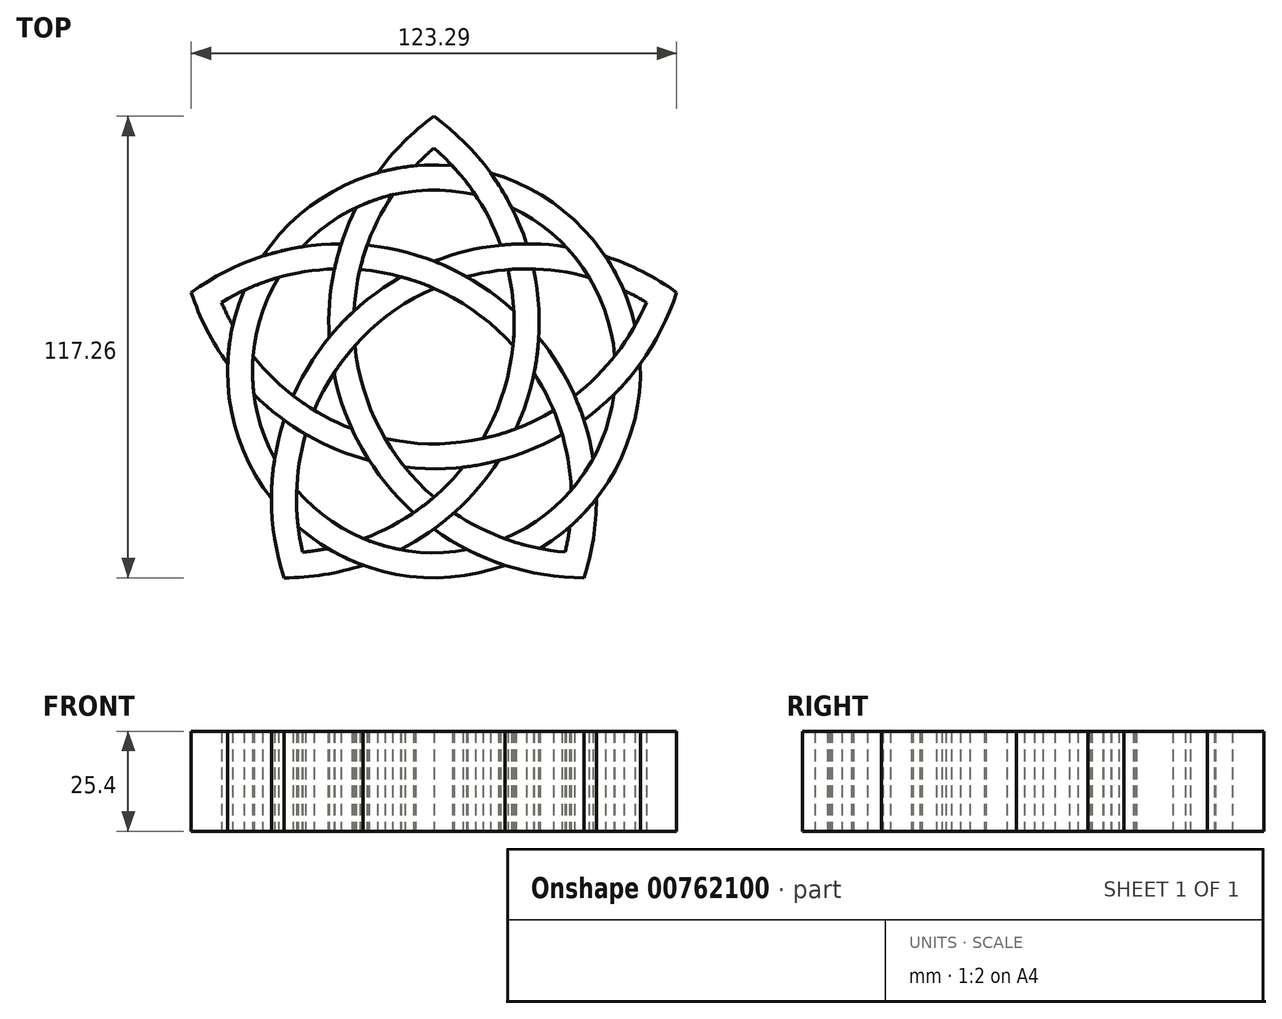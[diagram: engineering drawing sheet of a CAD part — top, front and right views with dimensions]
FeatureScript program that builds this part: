
annotation { "Feature Type Name" : "Feature", "Feature Type Description" : "" }
export const myFeature = defineFeature(function(context is Context, id is Id, definition is map)
    precondition{}
    {
        {
            var Q0;
            Q0=qCreatedBy(makeId("Top.planeOp"),FACE);
            var sketch = newSketch(context, id + "F0", { "sketchPlane" : qUnion([Q0])});
            skLineSegment(sketch, "E0", {"start": v(0, 72.47) * mm, "end": v(-61.65, 117.26) * mm, "construction": true});
            skLineSegment(sketch, "E1", {"start": v(-61.65, 117.26) * mm, "end": v(-123.3, 72.47) * mm, "construction": true});
            skLineSegment(sketch, "E2", {"start": v(-123.3, 72.47) * mm, "end": v(-99.75, 0) * mm, "construction": true});
            skLineSegment(sketch, "E3", {"start": v(-99.75, 0) * mm, "end": v(-23.55, 0) * mm, "construction": true});
            skLineSegment(sketch, "E4", {"start": v(0, 72.47) * mm, "end": v(-23.55, 0) * mm, "construction": true});
            skArc(sketch, "E5", {"start": v(-23.55, 0) * mm, "mid": v(-21.17, 9.92) * mm, "end": v(-20.37, 20.09) * mm});
            skArc(sketch, "E6", {"start": v(0, 72.47) * mm, "mid": v(-8.7, 77.8) * mm, "end": v(-18.13, 81.7) * mm});
            skArc(sketch, "E7", {"start": v(-99.75, 0) * mm, "mid": v(-89.58, 0.8) * mm, "end": v(-79.66, 3.2) * mm});
            skArc(sketch, "E8", {"start": v(-61.65, 117.26) * mm, "mid": v(-69.4, 110.63) * mm, "end": v(-76.02, 102.87) * mm});
            skArc(sketch, "E9", {"start": v(-123.3, 72.47) * mm, "mid": v(-119.39, 63.05) * mm, "end": v(-114.05, 54.35) * mm});
            skArc(sketch, "E10.0", {"start": v(-7.7, 69.97) * mm, "mid": v(-10.51, 71.58) * mm, "end": v(-13.42, 73.04) * mm});
            skArc(sketch, "E11.0", {"start": v(-28.3, 6.54) * mm, "mid": v(-27.64, 9.73) * mm, "end": v(-27.16, 12.94) * mm});
            skArc(sketch, "E12.0", {"start": v(-61.65, 109.17) * mm, "mid": v(-64.05, 106.99) * mm, "end": v(-66.33, 104.67) * mm});
            skArc(sketch, "E13.0", {"start": v(-95, 6.54) * mm, "mid": v(-91.76, 6.9) * mm, "end": v(-88.56, 7.43) * mm});
            skArc(sketch, "E14.0", {"start": v(-115.6, 69.97) * mm, "mid": v(-114.27, 67) * mm, "end": v(-112.77, 64.12) * mm});
            skPoint(sketch, "E15.first.point", {"position": v(-99.75, 40.06) * mm});
            skPoint(sketch, "E15.second.point", {"position": v(-38.1, 84.85) * mm});
            skPoint(sketch, "E15.third.point", {"position": v(-23.55, 40.06) * mm});
            skArc(sketch, "E16", {"start": v(-51.14, 97.32) * mm, "mid": v(-74.92, 96.58) * mm, "end": v(-95.16, 84.08) * mm});
            skArc(sketch, "E17.0", {"start": v(-56.96, 104.67) * mm, "mid": v(-84.2, 99.78) * mm, "end": v(-105.17, 81.7) * mm});
            skArc(sketch, "E18.trimOffspring", {"start": v(-85.2, 84.85) * mm, "mid": v(-105.22, 81.68) * mm, "end": v(-123.3, 72.47) * mm});
            skArc(sketch, "E19.trimOffspring", {"start": v(-86.91, 78.47) * mm, "mid": v(-101.81, 76.09) * mm, "end": v(-115.6, 69.97) * mm});
            skArc(sketch, "E20.trimOffspring", {"start": v(-81.72, 58.96) * mm, "mid": v(-75.4, 37.78) * mm, "end": v(-61.65, 20.47) * mm});
            skArc(sketch, "E21.trimOffspring", {"start": v(-87.08, 51.96) * mm, "mid": v(-79.8, 32.6) * mm, "end": v(-66.78, 16.53) * mm});
            skArc(sketch, "E22.trimOffspring", {"start": v(-74.05, 35.36) * mm, "mid": v(-51.95, 34.84) * mm, "end": v(-31.24, 42.56) * mm});
            skArc(sketch, "E23.trimOffspring", {"start": v(-69.05, 28.1) * mm, "mid": v(-48.4, 29.05) * mm, "end": v(-29.08, 36.46) * mm});
            skArc(sketch, "E24.trimOffspring", {"start": v(-56.51, 16.53) * mm, "mid": v(-43.06, 9.7) * mm, "end": v(-28.3, 6.54) * mm});
            skArc(sketch, "E25.trimOffspring", {"start": v(-61.65, 12.38) * mm, "mid": v(-43.58, 3.17) * mm, "end": v(-23.55, 0) * mm});
            skArc(sketch, "E26.trimOffspring", {"start": v(-23.55, 40.06) * mm, "mid": v(-9.2, 54.4) * mm, "end": v(0, 72.47) * mm});
            skArc(sketch, "E27.trimOffspring", {"start": v(-25.9, 46.23) * mm, "mid": v(-15.25, 56.91) * mm, "end": v(-7.7, 69.97) * mm});
            skArc(sketch, "E28.trimOffspring", {"start": v(-41.35, 67.77) * mm, "mid": v(-58.62, 79.15) * mm, "end": v(-78.6, 84.51) * mm});
            skArc(sketch, "E29.trimOffspring", {"start": v(-41.57, 58.96) * mm, "mid": v(-59.14, 72.38) * mm, "end": v(-80.44, 78.3) * mm});
            skArc(sketch, "E30.trimOffspring", {"start": v(-61.65, 73.55) * mm, "mid": v(-79.83, 60.98) * mm, "end": v(-92.05, 42.56) * mm});
            skArc(sketch, "E31.trimOffspring", {"start": v(-69.96, 76.48) * mm, "mid": v(-86.12, 63.57) * mm, "end": v(-97.39, 46.23) * mm});
            skArc(sketch, "E32.trimOffspring", {"start": v(-99.75, 40.06) * mm, "mid": v(-102.92, 20.03) * mm, "end": v(-99.75, 0) * mm});
            skArc(sketch, "E33.trimOffspring", {"start": v(-94.21, 36.46) * mm, "mid": v(-96.55, 21.55) * mm, "end": v(-95, 6.54) * mm});
            skArc(sketch, "E34.trimOffspring", {"start": v(-49.24, 35.36) * mm, "mid": v(-41.91, 56.22) * mm, "end": v(-42.85, 78.3) * mm});
            skArc(sketch, "E35.trimOffspring", {"start": v(-40.8, 37.88) * mm, "mid": v(-35.3, 57.82) * mm, "end": v(-36.38, 78.47) * mm});
            skArc(sketch, "E36.trimOffspring", {"start": v(-38.1, 84.85) * mm, "mid": v(-47.3, 102.92) * mm, "end": v(-61.65, 117.26) * mm});
            skArc(sketch, "E37.trimOffspring", {"start": v(-44.7, 84.51) * mm, "mid": v(-51.57, 97.95) * mm, "end": v(-61.65, 109.17) * mm});
            skArc(sketch, "E38.trimOffspring", {"start": v(-72.15, 97.32) * mm, "mid": v(-79.05, 83.2) * mm, "end": v(-81.94, 67.77) * mm});
            skArc(sketch, "E39.trimOffspring", {"start": v(-81.38, 94.1) * mm, "mid": v(-87, 78.04) * mm, "end": v(-88.26, 61.09) * mm});
            skArc(sketch, "E40.trimOffspring", {"start": v(-101.08, 76.3) * mm, "mid": v(-107.73, 53.46) * mm, "end": v(-102.1, 30.34) * mm});
            skArc(sketch, "E41.trimOffspring", {"start": v(-109.87, 73.04) * mm, "mid": v(-113.64, 45.61) * mm, "end": v(-102.92, 20.09) * mm});
            skArc(sketch, "E42.trimOffspring", {"start": v(-107.57, 56.32) * mm, "mid": v(-96.29, 45.4) * mm, "end": v(-82.5, 37.88) * mm});
            skArc(sketch, "E43.trimOffspring", {"start": v(-107.36, 46.54) * mm, "mid": v(-93.83, 36.24) * mm, "end": v(-78.1, 29.8) * mm});
            skArc(sketch, "E44.trimOffspring", {"start": v(-96.53, 22.31) * mm, "mid": v(-76.85, 8.93) * mm, "end": v(-53.13, 7.14) * mm});
            skArc(sketch, "E45.trimOffspring", {"start": v(-96.14, 12.94) * mm, "mid": v(-71.22, 0.88) * mm, "end": v(-43.63, 3.2) * mm});
            skArc(sketch, "E46.trimOffspring", {"start": v(-79.52, 9.96) * mm, "mid": v(-65.65, 17.32) * mm, "end": v(-54.24, 28.1) * mm});
            skArc(sketch, "E47.trimOffspring", {"start": v(-70.17, 7.14) * mm, "mid": v(-56.18, 16.82) * mm, "end": v(-45.2, 29.8) * mm});
            skArc(sketch, "E48.trimOffspring", {"start": v(-43.77, 9.96) * mm, "mid": v(-24.97, 24.53) * mm, "end": v(-15.94, 46.54) * mm});
            skArc(sketch, "E49.trimOffspring", {"start": v(-34.74, 7.43) * mm, "mid": v(-15.57, 27.4) * mm, "end": v(-9.24, 54.35) * mm});
            skArc(sketch, "E50.trimOffspring", {"start": v(-26.77, 22.31) * mm, "mid": v(-29.48, 37.78) * mm, "end": v(-36.22, 51.96) * mm});
            skArc(sketch, "E51.trimOffspring", {"start": v(-21.2, 30.34) * mm, "mid": v(-26.08, 46.63) * mm, "end": v(-35.04, 61.09) * mm});
            skArc(sketch, "E52.trimOffspring", {"start": v(-10.53, 64.12) * mm, "mid": v(-23.6, 88.53) * mm, "end": v(-47.27, 102.87) * mm});
            skArc(sketch, "E53.trimOffspring", {"start": v(-15.72, 56.32) * mm, "mid": v(-23.77, 78.7) * mm, "end": v(-41.91, 94.1) * mm});
            skArc(sketch, "E54.trimOffspring", {"start": v(-22.21, 76.3) * mm, "mid": v(-37.76, 78.5) * mm, "end": v(-53.34, 76.48) * mm});
            skArc(sketch, "E55.trimOffspring", {"start": v(-28.13, 84.08) * mm, "mid": v(-45.13, 84.47) * mm, "end": v(-61.65, 80.42) * mm});
            skSolve(sketch);
        }
        {
            var Q0;
            {var subQ2=sQuery(id+"F0.wireOp",EDGE,"E37.trimOffspring");var subQ5=sQuery(id+"F0.wireOp",EDGE,"E16");var subQ9=makeQuery(id+"F0.imprint","INTERSECT",VERTEX,{"derivedFrom":[subQ5,subQ2]});Q0=makeQuery(id+"F0.imprint","IMPRINT",FACE,{"disambiguationData":[TD([[makeQuery(id+"F0.imprint","IMPRINT",EDGE,{"disambiguationData":[TD([[subQ9,-1.0]])],"derivedFrom":subQ5}),-1.0]])]});}
            extrude(context, id + "F1", {"entities" : qUnion([Q0]), "depth" : 25.4 * mm, "offsetDistance" : 25.4 * mm});
        }
        {
            var Q0;
            {var subQ0=sQuery(id+"F0.wireOp",EDGE,"E40.trimOffspring");var subQ3=sQuery(id+"F0.wireOp",EDGE,"E19.trimOffspring");var subQ4=makeQuery(id+"F0.imprint","INTERSECT",VERTEX,{"derivedFrom":[subQ3,subQ0]});Q0=makeQuery(id+"F0.imprint","IMPRINT",FACE,{"disambiguationData":[TD([[makeQuery(id+"F0.imprint","IMPRINT",EDGE,{"disambiguationData":[TD([[subQ4,-1.0]])],"derivedFrom":subQ3}),1.0]])]});}
            extrude(context, id + "F2", {"entities" : qUnion([Q0]), "depth" : 25.4 * mm, "offsetDistance" : 25.4 * mm});
        }
        {
            var Q0;
            {var subQ0=sQuery(id+"F0.wireOp",EDGE,"E44.trimOffspring");var subQ7=sQuery(id+"F0.wireOp",EDGE,"E25.trimOffspring");var subQ8=makeQuery(id+"F0.imprint","INTERSECT",VERTEX,{"derivedFrom":[subQ7,subQ0]});Q0=makeQuery(id+"F0.imprint","IMPRINT",FACE,{"disambiguationData":[TD([[makeQuery(id+"F0.imprint","IMPRINT",EDGE,{"disambiguationData":[TD([[subQ8,-1.0]])],"derivedFrom":subQ7}),-1.0]])]});}
            extrude(context, id + "F3", {"entities" : qUnion([Q0]), "depth" : 25.4 * mm, "offsetDistance" : 25.4 * mm});
        }
        {
            var Q0;
            {var subQ0=sQuery(id+"F0.wireOp",EDGE,"E48.trimOffspring");var subQ7=sQuery(id+"F0.wireOp",EDGE,"E24.trimOffspring");var subQ8=makeQuery(id+"F0.imprint","INTERSECT",VERTEX,{"derivedFrom":[subQ7,subQ0]});Q0=makeQuery(id+"F0.imprint","IMPRINT",FACE,{"disambiguationData":[TD([[makeQuery(id+"F0.imprint","IMPRINT",EDGE,{"disambiguationData":[TD([[subQ8,-1.0]])],"derivedFrom":subQ7}),1.0]])]});}
            extrude(context, id + "F4", {"entities" : qUnion([Q0]), "depth" : 25.4 * mm, "offsetDistance" : 25.4 * mm});
        }
        {
            var Q0;
            {var subQ0=sQuery(id+"F0.wireOp",EDGE,"E52.trimOffspring");var subQ2=sQuery(id+"F0.wireOp",EDGE,"E27.trimOffspring");var subQ3=makeQuery(id+"F0.imprint","INTERSECT",VERTEX,{"derivedFrom":[subQ2,subQ0]});Q0=makeQuery(id+"F0.imprint","IMPRINT",FACE,{"disambiguationData":[TD([[makeQuery(id+"F0.imprint","IMPRINT",EDGE,{"disambiguationData":[TD([[subQ3,1.0]])],"derivedFrom":subQ2}),1.0]])]});}
            extrude(context, id + "F5", {"entities" : qUnion([Q0]), "depth" : 25.4 * mm, "offsetDistance" : 25.4 * mm});
        }
        {
            var Q0;
            {var subQ5=sQuery(id+"F0.wireOp",EDGE,"E8");Q0=makeQuery(id+"F0.imprint","IMPRINT",FACE,{"disambiguationData":[TD([[makeQuery(id+"F0.imprint","IMPRINT",EDGE,{"derivedFrom":subQ5}),1.0]])]});}
            extrude(context, id + "F6", {"entities" : qUnion([Q0]), "depth" : 25.4 * mm, "offsetDistance" : 25.4 * mm});
        }
        {
            var Q0;
            {var subQ0=sQuery(id+"F0.wireOp",EDGE,"E38.trimOffspring");var subQ3=sQuery(id+"F0.wireOp",EDGE,"E16");var subQ4=makeQuery(id+"F0.imprint","INTERSECT",VERTEX,{"derivedFrom":[subQ3,subQ0]});Q0=makeQuery(id+"F0.imprint","IMPRINT",FACE,{"disambiguationData":[TD([[makeQuery(id+"F0.imprint","IMPRINT",EDGE,{"disambiguationData":[TD([[subQ4,-1.0]])],"derivedFrom":subQ3}),1.0]])]});}
            extrude(context, id + "F7", {"entities" : qUnion([Q0]), "depth" : 25.4 * mm, "offsetDistance" : 25.4 * mm});
        }
        {
            var Q0;
            {var subQ0=sQuery(id+"F0.wireOp",EDGE,"E30.trimOffspring");var subQ5=sQuery(id+"F0.wireOp",EDGE,"E20.trimOffspring");var subQ10=makeQuery(id+"F0.imprint","INTERSECT",VERTEX,{"derivedFrom":[subQ5,subQ0]});Q0=makeQuery(id+"F0.imprint","IMPRINT",FACE,{"disambiguationData":[TD([[makeQuery(id+"F0.imprint","IMPRINT",EDGE,{"disambiguationData":[TD([[subQ10,-1.0]])],"derivedFrom":subQ5}),-1.0]])]});}
            extrude(context, id + "F8", {"entities" : qUnion([Q0]), "depth" : 25.4 * mm, "offsetDistance" : 25.4 * mm});
        }
        {
            var Q0;
            {var subQ6=sQuery(id+"F0.wireOp",EDGE,"E5");Q0=makeQuery(id+"F0.imprint","IMPRINT",FACE,{"disambiguationData":[TD([[makeQuery(id+"F0.imprint","IMPRINT",EDGE,{"derivedFrom":subQ6}),1.0]])]});}
            extrude(context, id + "F9", {"entities" : qUnion([Q0]), "depth" : 25.4 * mm, "offsetDistance" : 25.4 * mm});
        }
        {
            var Q0;
            {var subQ0=sQuery(id+"F0.wireOp",EDGE,"E50.trimOffspring");var subQ4=sQuery(id+"F0.wireOp",EDGE,"E35.trimOffspring");var subQ5=makeQuery(id+"F0.imprint","INTERSECT",VERTEX,{"derivedFrom":[subQ4,subQ0]});Q0=makeQuery(id+"F0.imprint","IMPRINT",FACE,{"disambiguationData":[TD([[makeQuery(id+"F0.imprint","IMPRINT",EDGE,{"disambiguationData":[TD([[subQ5,-1.0]])],"derivedFrom":subQ4}),-1.0]])]});}
            extrude(context, id + "F10", {"entities" : qUnion([Q0]), "depth" : 25.4 * mm, "offsetDistance" : 25.4 * mm});
        }
        {
            var Q0;
            {var subQ0=sQuery(id+"F0.wireOp",EDGE,"E34.trimOffspring");var subQ5=sQuery(id+"F0.wireOp",EDGE,"E28.trimOffspring");var subQ9=makeQuery(id+"F0.imprint","INTERSECT",VERTEX,{"derivedFrom":[subQ5,subQ0]});Q0=makeQuery(id+"F0.imprint","IMPRINT",FACE,{"disambiguationData":[TD([[makeQuery(id+"F0.imprint","IMPRINT",EDGE,{"disambiguationData":[TD([[subQ9,-1.0]])],"derivedFrom":subQ5}),1.0]])]});}
            extrude(context, id + "F11", {"entities" : qUnion([Q0]), "depth" : 25.4 * mm, "offsetDistance" : 25.4 * mm});
        }
        {
            var Q0;
            {var subQ10=sQuery(id+"F0.wireOp",EDGE,"E9");Q0=makeQuery(id+"F0.imprint","IMPRINT",FACE,{"disambiguationData":[TD([[makeQuery(id+"F0.imprint","IMPRINT",EDGE,{"derivedFrom":subQ10}),1.0]])]});}
            extrude(context, id + "F12", {"entities" : qUnion([Q0]), "depth" : 25.4 * mm, "offsetDistance" : 25.4 * mm});
        }
        {
            var Q0;
            {var subQ0=sQuery(id+"F0.wireOp",EDGE,"E42.trimOffspring");var subQ7=sQuery(id+"F0.wireOp",EDGE,"E21.trimOffspring");var subQ8=makeQuery(id+"F0.imprint","INTERSECT",VERTEX,{"derivedFrom":[subQ7,subQ0]});Q0=makeQuery(id+"F0.imprint","IMPRINT",FACE,{"disambiguationData":[TD([[makeQuery(id+"F0.imprint","IMPRINT",EDGE,{"disambiguationData":[TD([[subQ8,-1.0]])],"derivedFrom":subQ7}),-1.0]])]});}
            extrude(context, id + "F13", {"entities" : qUnion([Q0]), "depth" : 25.4 * mm, "offsetDistance" : 25.4 * mm});
        }
        {
            var Q0;
            {var subQ1=sQuery(id+"F0.wireOp",EDGE,"E22.trimOffspring");var subQ5=sQuery(id+"F0.wireOp",EDGE,"E20.trimOffspring");var subQ6=makeQuery(id+"F0.imprint","INTERSECT",VERTEX,{"derivedFrom":[subQ5,subQ1]});Q0=makeQuery(id+"F0.imprint","IMPRINT",FACE,{"disambiguationData":[TD([[makeQuery(id+"F0.imprint","IMPRINT",EDGE,{"disambiguationData":[TD([[subQ6,-1.0]])],"derivedFrom":subQ5}),1.0]])]});}
            extrude(context, id + "F14", {"entities" : qUnion([Q0]), "depth" : 25.4 * mm, "offsetDistance" : 25.4 * mm});
        }
        {
            var Q0;
            {var subQ6=sQuery(id+"F0.wireOp",EDGE,"E6");Q0=makeQuery(id+"F0.imprint","IMPRINT",FACE,{"disambiguationData":[TD([[makeQuery(id+"F0.imprint","IMPRINT",EDGE,{"derivedFrom":subQ6}),1.0]])]});}
            extrude(context, id + "F15", {"entities" : qUnion([Q0]), "depth" : 25.4 * mm, "offsetDistance" : 25.4 * mm});
        }
        {
            var Q0;
            {var subQ0=sQuery(id+"F0.wireOp",EDGE,"E54.trimOffspring");var subQ5=sQuery(id+"F0.wireOp",EDGE,"E28.trimOffspring");var subQ6=makeQuery(id+"F0.imprint","INTERSECT",VERTEX,{"derivedFrom":[subQ5,subQ0]});Q0=makeQuery(id+"F0.imprint","IMPRINT",FACE,{"disambiguationData":[TD([[makeQuery(id+"F0.imprint","IMPRINT",EDGE,{"disambiguationData":[TD([[subQ6,-1.0]])],"derivedFrom":subQ5}),-1.0]])]});}
            extrude(context, id + "F16", {"entities" : qUnion([Q0]), "depth" : 25.4 * mm, "offsetDistance" : 25.4 * mm});
        }
        {
            var Q0;
            {var subQ0=sQuery(id+"F0.wireOp",EDGE,"E30.trimOffspring");var subQ5=sQuery(id+"F0.wireOp",EDGE,"E29.trimOffspring");var subQ6=makeQuery(id+"F0.imprint","INTERSECT",VERTEX,{"derivedFrom":[subQ5,subQ0]});Q0=makeQuery(id+"F0.imprint","IMPRINT",FACE,{"disambiguationData":[TD([[makeQuery(id+"F0.imprint","IMPRINT",EDGE,{"disambiguationData":[TD([[subQ6,-1.0]])],"derivedFrom":subQ5}),1.0]])]});}
            extrude(context, id + "F17", {"entities" : qUnion([Q0]), "depth" : 25.4 * mm, "offsetDistance" : 25.4 * mm});
        }
        {
            var Q0;
            {var subQ10=sQuery(id+"F0.wireOp",EDGE,"E7");Q0=makeQuery(id+"F0.imprint","IMPRINT",FACE,{"disambiguationData":[TD([[makeQuery(id+"F0.imprint","IMPRINT",EDGE,{"derivedFrom":subQ10}),1.0]])]});}
            extrude(context, id + "F18", {"entities" : qUnion([Q0]), "depth" : 25.4 * mm, "offsetDistance" : 25.4 * mm});
        }
        {
            var Q0;
            {var subQ0=sQuery(id+"F0.wireOp",EDGE,"E46.trimOffspring");var subQ7=sQuery(id+"F0.wireOp",EDGE,"E23.trimOffspring");var subQ8=makeQuery(id+"F0.imprint","INTERSECT",VERTEX,{"derivedFrom":[subQ7,subQ0]});Q0=makeQuery(id+"F0.imprint","IMPRINT",FACE,{"disambiguationData":[TD([[makeQuery(id+"F0.imprint","IMPRINT",EDGE,{"disambiguationData":[TD([[subQ8,-1.0]])],"derivedFrom":subQ7}),-1.0]])]});}
            extrude(context, id + "F19", {"entities" : qUnion([Q0]), "depth" : 25.4 * mm, "offsetDistance" : 25.4 * mm});
        }
        {
            var Q0;
            {var subQ0=sQuery(id+"F0.wireOp",EDGE,"E34.trimOffspring");var subQ5=sQuery(id+"F0.wireOp",EDGE,"E22.trimOffspring");var subQ6=makeQuery(id+"F0.imprint","INTERSECT",VERTEX,{"derivedFrom":[subQ5,subQ0]});Q0=makeQuery(id+"F0.imprint","IMPRINT",FACE,{"disambiguationData":[TD([[makeQuery(id+"F0.imprint","IMPRINT",EDGE,{"disambiguationData":[TD([[subQ6,-1.0]])],"derivedFrom":subQ5}),1.0]])]});}
            extrude(context, id + "F20", {"entities" : qUnion([Q0]), "depth" : 25.4 * mm, "offsetDistance" : 25.4 * mm});
        }
    });
